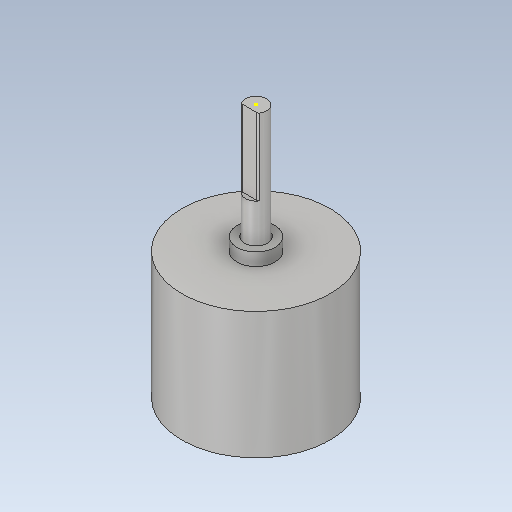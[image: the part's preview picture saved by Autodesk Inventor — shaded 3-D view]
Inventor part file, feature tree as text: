
AUTODESK INVENTOR PART (.ipt)
format: ipt  version: 2020 (Build 240168000, 168)  size: 148,992 bytes
history: native  units: mm
features: sketch x7, extrude x6, fillet x1, projected_geometry x1
ambient origin geometry x8: Origin, YZ Plane, XZ Plane, XY Plane, X Axis, Y Axis, Z Axis, Center Point
bodies: Solid1 (feature_tree)
feature tree (15):
  extrude  "Extrusion1"  Depth=30.0mm TaperAngle=0.0deg
  extrude  "Extrusion2"  Depth=2.0mm TaperAngle=0.0deg
  extrude  "Extrusion3"  Depth=30.0mm TaperAngle=0.0deg
  extrude  "Extrusion5"  Depth=9.0mm
  extrude  "Extrusion6"  Depth=3.0mm
  extrude  "Extrusion7"  Depth=0.5mm TaperAngle=0.0deg
  fillet  "Fillet1"  Radius=1.5mm
  sketch  "Sketch7"  dims[d20=18.0mm d21=0.0mm d22=0.5mm]
  sketch  "Sketch1"  dims[d0=35.0mm d1=30.0mm d2=0.0mm]
  sketch  "Sketch2"  dims[d3=5.0mm d4=2.0mm d5=0.0mm]
  sketch  "Sketch3"  dims[d6=5.0mm d7=30.0mm d8=0.0mm]
  sketch  "Sketch4"  dims[d9=9.0mm d12=5.5mm]
  sketch  "Sketch5"  dims[d13=3.0mm d14=0.0mm d15=5.5mm]
  sketch  "Sketch6"  dims[d16=9.0mm d17=0.5mm d18=0.0mm d19=1.5mm]
  projected_geometry  "Projected Loop1"
